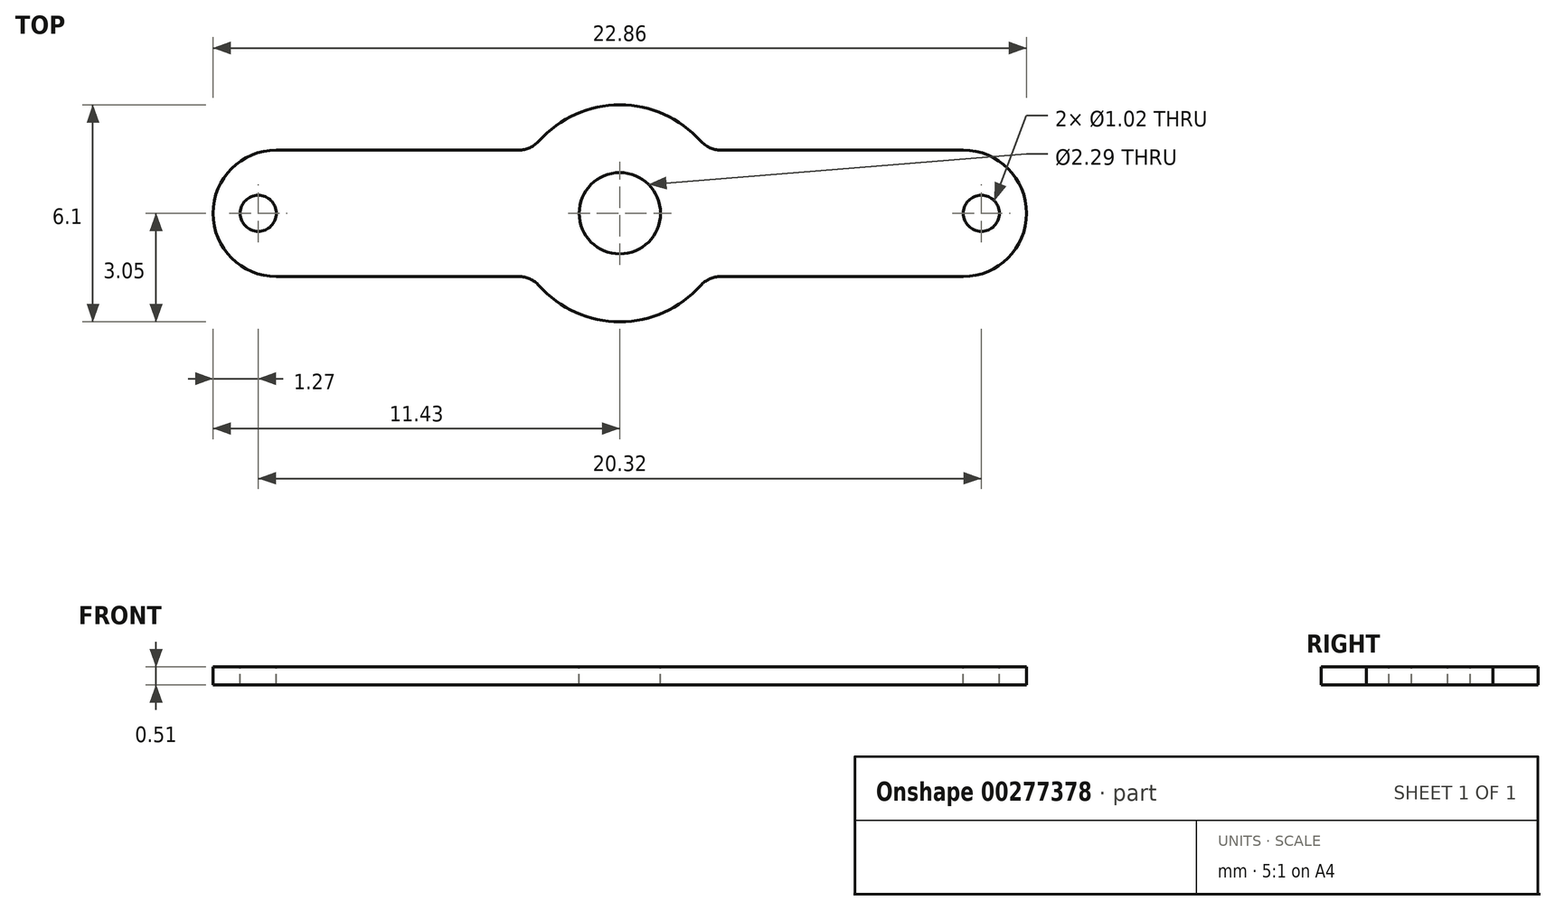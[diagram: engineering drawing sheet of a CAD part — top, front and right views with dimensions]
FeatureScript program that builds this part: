
annotation { "Feature Type Name" : "Feature", "Feature Type Description" : "" }
export const myFeature = defineFeature(function(context is Context, id is Id, definition is map)
    precondition{}
    {
        {
            var Q0;
            Q0=qCreatedBy(makeId("Top.planeOp"),FACE);
            var sketch = newSketch(context, id + "F0", { "sketchPlane" : qUnion([Q0])});
            skLineSegment(sketch, "E0.bottom", {"start": v(-9.65, 1.78) * mm, "end": v(-2.48, 1.78) * mm});
            skLineSegment(sketch, "E0.top", {"start": v(-9.65, -1.78) * mm, "end": v(-2.48, -1.78) * mm});
            skLineSegment(sketch, "E0.left", {"start": v(-11.43, 0) * mm, "end": v(-11.43, 0) * mm});
            skLineSegment(sketch, "E0.right", {"start": v(11.43, 0) * mm, "end": v(11.43, 0) * mm});
            skPoint(sketch, "E1.visualSharp", {"position": v(-11.43, -1.78) * mm});
            skArc(sketch, "E1.filletArc", {"start": v(-11.43, 0) * mm, "mid": v(-10.9, -1.26) * mm, "end": v(-9.65, -1.78) * mm});
            skPoint(sketch, "E2.visualSharp", {"position": v(-11.43, 1.78) * mm});
            skArc(sketch, "E2.filletArc", {"start": v(-9.65, 1.78) * mm, "mid": v(-10.9, 1.26) * mm, "end": v(-11.43, 0) * mm});
            skPoint(sketch, "E3.visualSharp", {"position": v(11.43, 1.78) * mm});
            skArc(sketch, "E3.filletArc", {"start": v(11.43, 0) * mm, "mid": v(10.9, 1.26) * mm, "end": v(9.65, 1.78) * mm});
            skPoint(sketch, "E4.visualSharp", {"position": v(11.43, -1.78) * mm});
            skArc(sketch, "E4.filletArc", {"start": v(9.65, -1.78) * mm, "mid": v(10.9, -1.26) * mm, "end": v(11.43, 0) * mm});
            skArc(sketch, "E5", {"start": v(-2.48, -1.78) * mm, "mid": v(0, -3.05) * mm, "end": v(2.48, -1.78) * mm});
            skLineSegment(sketch, "E6.trimOffspring", {"start": v(2.48, 1.78) * mm, "end": v(9.65, 1.78) * mm});
            skLineSegment(sketch, "E7.trimOffspring", {"start": v(2.48, -1.78) * mm, "end": v(9.65, -1.78) * mm});
            skArc(sketch, "E8.trimOffspring", {"start": v(2.48, 1.78) * mm, "mid": v(0, 3.05) * mm, "end": v(-2.48, 1.78) * mm});
            skSolve(sketch);
        }
        {
            var Q0;
            Q0 = qSketchRegion(id + "F0", true);
            extrude(context, id + "F1", {"entities" : qUnion([Q0]), "depth" : 0.5 * mm});
        }
        {
            var Q0;
            Q0=makeQuery(id+"F1.opExtrude","CAP_FACE",FACE,{"disambiguationData":[OSD([sQuery(id+"F0.wireOp",EDGE,"E0.bottom"),sQuery(id+"F0.wireOp",EDGE,"E0.top"),sQuery(id+"F0.wireOp",EDGE,"E1.filletArc"),sQuery(id+"F0.wireOp",EDGE,"E2.filletArc"),sQuery(id+"F0.wireOp",EDGE,"E3.filletArc"),sQuery(id+"F0.wireOp",EDGE,"E4.filletArc")])],"isStart":false});
            var sketch = newSketch(context, id + "F2", { "sketchPlane" : qUnion([Q0])});
            skCircle(sketch, "E9", {"center": v(-10.16, 0) * mm, "radius": 0.5 * mm});
            skCircle(sketch, "E10", {"center": v(10.16, 0) * mm, "radius": 0.5 * mm});
            skCircle(sketch, "E11", {"center": v(0, 0) * mm, "radius": 1.14 * mm});
            skSolve(sketch);
        }
        {
            var Q0;
            Q0 = qSketchRegion(id + "F2", true);
            extrude(context, id + "F3", {"entities" : qUnion([Q0]), "operationType" : NewBodyOperationType.REMOVE, "endBound" : BoundingType.THROUGH_ALL, "oppositeDirection" : true, "depth" : 25.4 * mm});
        }
        {
            var Q0;
            Q0=makeQuery(id+"F1.opExtrude","SWEPT_EDGE",EDGE,{"disambiguationData":[OSD([sQuery(id+"F0.wireOp",EDGE,"E0.top"),sQuery(id+"F0.wireOp",EDGE,"E5")])]});
            var Q1;
            Q1=makeQuery(id+"F1.opExtrude","SWEPT_EDGE",EDGE,{"disambiguationData":[OSD([sQuery(id+"F0.wireOp",EDGE,"E5"),sQuery(id+"F0.wireOp",EDGE,"E7.trimOffspring")])]});
            var Q2;
            Q2=makeQuery(id+"F1.opExtrude","SWEPT_EDGE",EDGE,{"disambiguationData":[OSD([sQuery(id+"F0.wireOp",EDGE,"E0.bottom"),sQuery(id+"F0.wireOp",EDGE,"E8.trimOffspring")])]});
            var Q3;
            Q3=makeQuery(id+"F1.opExtrude","SWEPT_EDGE",EDGE,{"disambiguationData":[OSD([sQuery(id+"F0.wireOp",EDGE,"E6.trimOffspring"),sQuery(id+"F0.wireOp",EDGE,"E8.trimOffspring")])]});
            fillet(context, id + "F4", {"entities" : qUnion([Q0, Q1, Q2, Q3]), "radius" : 0.76 * mm, "tangentPropagation" : true, "allowEdgeOverflow" : false});
        }
    });
